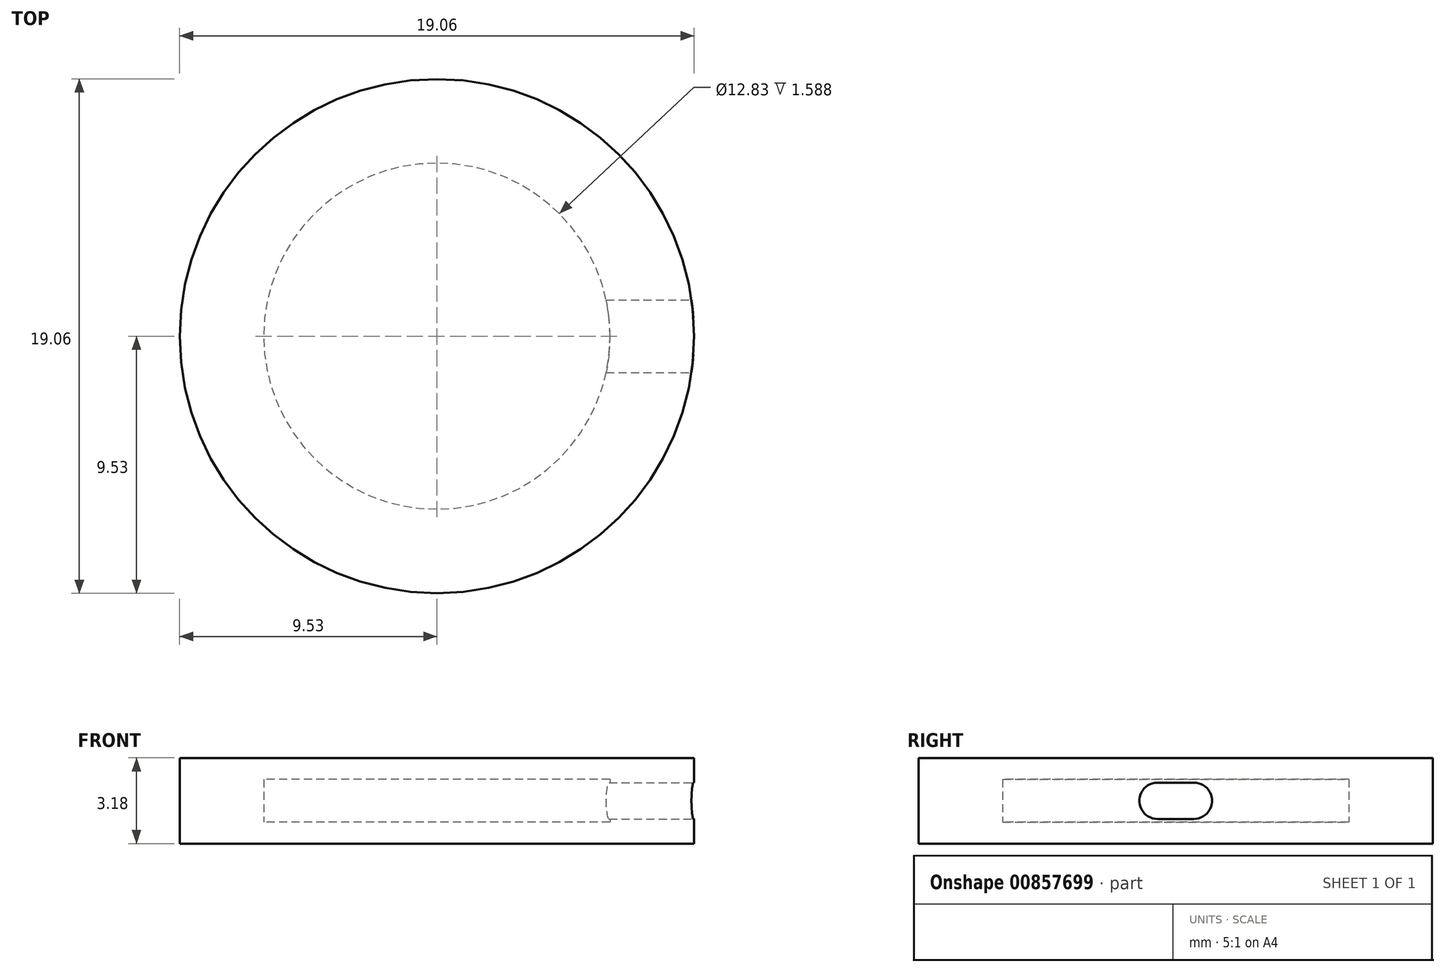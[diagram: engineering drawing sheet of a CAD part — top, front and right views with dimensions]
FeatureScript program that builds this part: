
annotation { "Feature Type Name" : "Feature", "Feature Type Description" : "" }
export const myFeature = defineFeature(function(context is Context, id is Id, definition is map)
    precondition{}
    {
        {
            var Q0;
            Q0=qCreatedBy(makeId("Top.planeOp"),FACE);
            var sketch = newSketch(context, id + "F0", { "sketchPlane" : qUnion([Q0])});
            skCircle(sketch, "E0", {"center": v(0, 0) * mm, "radius": 9.53 * mm});
            skSolve(sketch);
        }
        {
            var Q0;
            Q0=makeQuery(id+"F0.imprint","IMPRINT",FACE,{"disambiguationData":[TD([[makeQuery(id+"F0.imprint","IMPRINT",EDGE,{"derivedFrom":sQuery(id+"F0.wireOp",EDGE,"E0")}),1.0]])]});
            extrude(context, id + "F1", {"entities" : qUnion([Q0]), "depth" : 0.8 * mm, "offsetDistance" : 25.4 * mm});
        }
        {
            var Q0;
            Q0=makeQuery(id+"F1.opExtrude","CAP_FACE",FACE,{"disambiguationData":[OSD([sQuery(id+"F0.wireOp",EDGE,"E0")])],"isStart":false});
            var sketch = newSketch(context, id + "F2", { "sketchPlane" : qUnion([Q0])});
            skCircle(sketch, "E1", {"center": v(0, 0) * mm, "radius": 6.41 * mm});
            skSolve(sketch);
        }
        {
            var Q0;
            Q0=makeQuery(id+"F2.imprint","IMPRINT",FACE,{"disambiguationData":[TD([[makeQuery(id+"F2.imprint","IMPRINT",EDGE,{"derivedFrom":sQuery(id+"F2.wireOp",EDGE,"E1")}),-1.0]])]});
            extrude(context, id + "F3", {"entities" : qUnion([Q0]), "operationType" : NewBodyOperationType.ADD, "depth" : 1.59 * mm, "offsetDistance" : 25.4 * mm});
        }
        {
            var Q0;
            Q0=makeQuery(id+"F3.opExtrude","CAP_FACE",FACE,{"disambiguationData":[OSD([sQuery(id+"F0.wireOp",EDGE,"E0"),sQuery(id+"F2.wireOp",EDGE,"E1")])],"isStart":false});
            var sketch = newSketch(context, id + "F4", { "sketchPlane" : qUnion([Q0])});
            skCircle(sketch, "E2", {"center": v(0, 0) * mm, "radius": 9.53 * mm});
            skPoint(sketch, "E2.first.point", {"position": v(-8.62, 4.06) * mm});
            skPoint(sketch, "E2.second.point", {"position": v(-3.05, -9.02) * mm});
            skPoint(sketch, "E2.third.point", {"position": v(7.43, 5.96) * mm});
            skSolve(sketch);
        }
        {
            var Q0;
            Q0 = qSketchRegion(id + "F4", true);
            extrude(context, id + "F5", {"entities" : qUnion([Q0]), "operationType" : NewBodyOperationType.ADD, "depth" : 0.8 * mm, "offsetDistance" : 25.4 * mm});
        }
        {
            var Q0;
            Q0=qCreatedBy(makeId("Right.planeOp"),FACE);
            cPlane(context, id + "F6", {"entities" : qUnion([Q0]), "cplaneType" : CPlaneType.OFFSET, "offset" : 9.52 * mm, "width" : 152.4 * mm, "height" : 152.4 * mm});
        }
        {
            var Q0;
            Q0=qCreatedBy(id+"F6.planeOp",FACE);
            var sketch = newSketch(context, id + "F7", { "sketchPlane" : qUnion([Q0])});
            skLineSegment(sketch, "E3", {"start": v(0, 3.18) * mm, "end": v(0, 0) * mm, "construction": true});
            skLineSegment(sketch, "E4.bottom", {"start": v(-0.67, 2.26) * mm, "end": v(0.67, 2.26) * mm});
            skLineSegment(sketch, "E4.top", {"start": v(-0.67, 0.91) * mm, "end": v(0.67, 0.91) * mm});
            skLineSegment(sketch, "E5", {"start": v(0, 1.59) * mm, "end": v(0.67, 1.59) * mm, "construction": true});
            skArc(sketch, "E6", {"start": v(-0.67, 2.26) * mm, "mid": v(-1.35, 1.59) * mm, "end": v(-0.67, 0.91) * mm});
            skArc(sketch, "E7", {"start": v(0.67, 2.26) * mm, "mid": v(1.35, 1.59) * mm, "end": v(0.67, 0.91) * mm});
            skSolve(sketch);
        }
        {
            var Q0;
            Q0=makeQuery(id+"F7.imprint","IMPRINT",FACE,{"disambiguationData":[TD([[makeQuery(id+"F7.imprint","IMPRINT",EDGE,{"derivedFrom":sQuery(id+"F7.wireOp",EDGE,"E4.bottom")}),-1.0]])]});
            extrude(context, id + "F8", {"entities" : qUnion([Q0]), "operationType" : NewBodyOperationType.REMOVE, "oppositeDirection" : true, "depth" : 12.7 * mm, "offsetDistance" : 25.4 * mm});
        }
        {
            var Q0;
            Q0=qCreatedBy(makeId("Right.planeOp"),FACE);
            var sketch = newSketch(context, id + "F9", { "sketchPlane" : qUnion([Q0])});
            skLineSegment(sketch, "E8", {"start": v(0, 77.2) * mm, "end": v(0, -76.81) * mm});
            skSolve(sketch);
        }
        {
            var Q0;
            Q0=sQuery(id+"F9.wireOp",EDGE,"E8");
            cPlane(context, id + "F10", {"entities" : qUnion([Q0]), "cplaneType" : CPlaneType.LINE_ANGLE, "offset" : 25.4 * mm, "angle" : 15 * degree, "width" : 152.4 * mm, "height" : 152.4 * mm});
        }
        {
            var Q0;
            Q0=qCreatedBy(id+"F10.planeOp",FACE);
            cPlane(context, id + "F11", {"entities" : qUnion([Q0]), "cplaneType" : CPlaneType.OFFSET, "offset" : 9.52 * mm, "oppositeDirection" : true, "width" : 152.4 * mm, "height" : 152.4 * mm});
        }
    });
